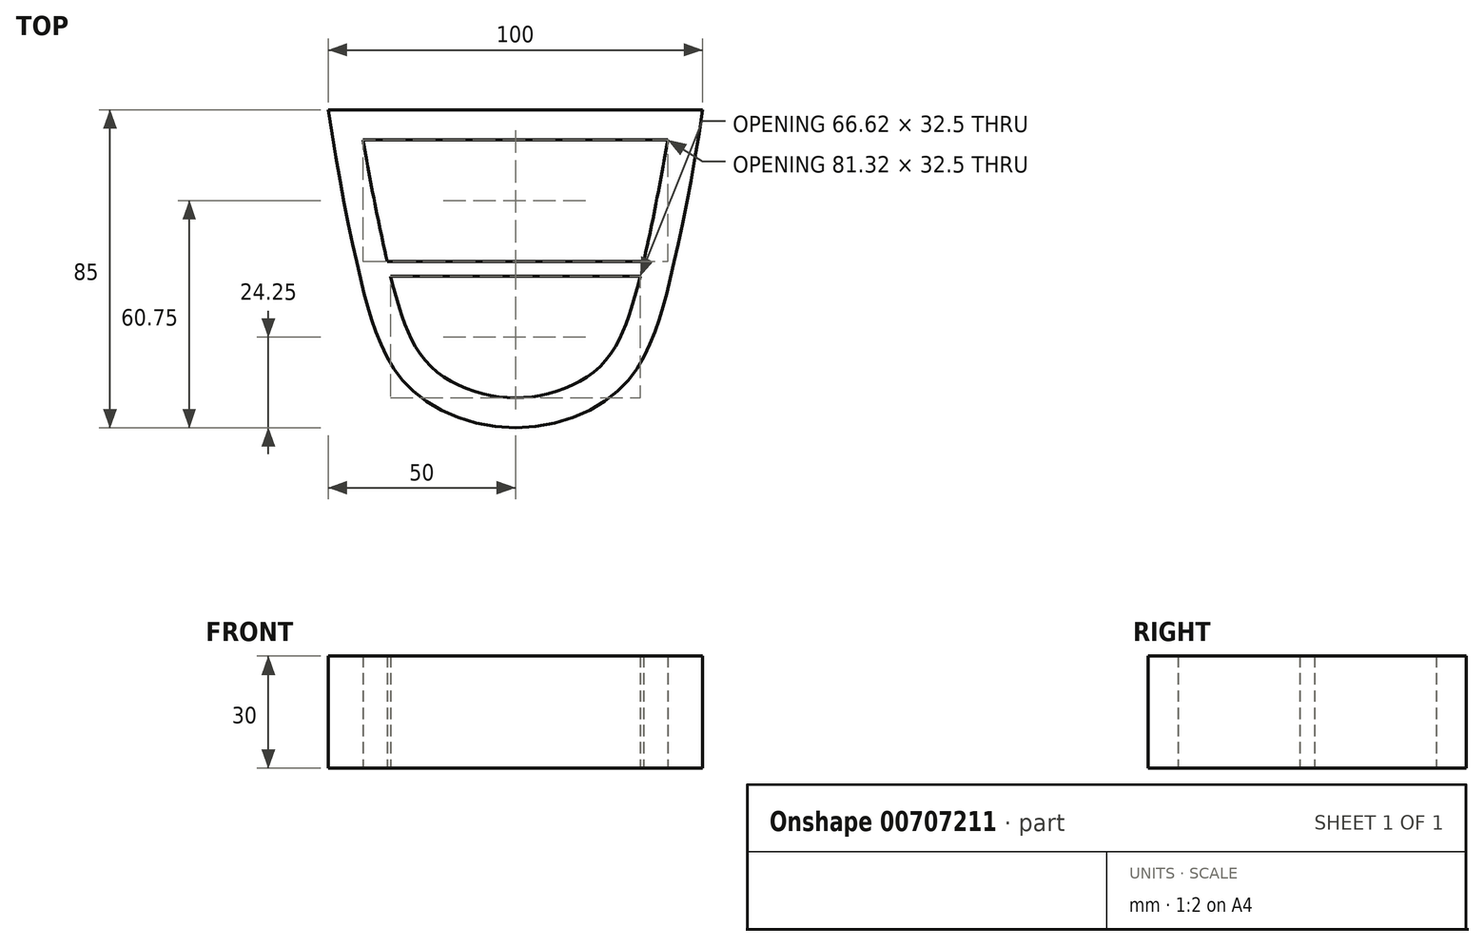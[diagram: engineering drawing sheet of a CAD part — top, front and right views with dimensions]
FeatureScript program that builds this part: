
annotation { "Feature Type Name" : "Feature", "Feature Type Description" : "" }
export const myFeature = defineFeature(function(context is Context, id is Id, definition is map)
    precondition{}
    {
        {
            var Q0;
            Q0=qCreatedBy(makeId("Top.planeOp"),FACE);
            var sketch = newSketch(context, id + "F0", { "sketchPlane" : qUnion([Q0])});
            skLineSegment(sketch, "E0.bottom", {"start": v(50, 42.5) * mm, "end": v(-50, 42.5) * mm});
            skLineSegment(sketch, "E0.top", {"start": v(50, -42.5) * mm, "end": v(-50, -42.5) * mm, "construction": true});
            skLineSegment(sketch, "E0.left", {"start": v(50, 42.5) * mm, "end": v(50, -42.5) * mm, "construction": true});
            skLineSegment(sketch, "E0.right", {"start": v(-50, 42.5) * mm, "end": v(-50, -42.5) * mm, "construction": true});
            skPoint(sketch, "E0.middle", {"position": v(0, 0) * mm});
            skPoint(sketch, "E1", {"position": v(0, -42.5) * mm});
            skPoint(sketch, "E2", {"position": v(-50, 0) * mm});
            skPoint(sketch, "E3", {"position": v(50, 0) * mm});
            skLineSegment(sketch, "E4", {"start": v(-50, 0) * mm, "end": v(-42, 0) * mm, "construction": true});
            skLineSegment(sketch, "E5", {"start": v(-42, 0) * mm, "end": v(42, 0) * mm, "construction": true});
            skLineSegment(sketch, "E6", {"start": v(42, 0) * mm, "end": v(50, 0) * mm, "construction": true});
            skLineSegment(sketch, "E7", {"start": v(-50, 0) * mm, "end": v(-50, -17.5) * mm, "construction": true});
            skLineSegment(sketch, "E8", {"start": v(-50, -17.5) * mm, "end": v(-37, -17.5) * mm, "construction": true});
            skLineSegment(sketch, "E9", {"start": v(-37, -17.5) * mm, "end": v(37, -17.5) * mm, "construction": true});
            skLineSegment(sketch, "E10", {"start": v(-50, -42.5) * mm, "end": v(-50, -32.5) * mm, "construction": true});
            skLineSegment(sketch, "E11", {"start": v(-50, -32.5) * mm, "end": v(-27.5, -32.5) * mm, "construction": true});
            skLineSegment(sketch, "E12", {"start": v(-27.5, -32.5) * mm, "end": v(27.5, -32.5) * mm, "construction": true});
            skFitSpline(sketch, "E13", {"points": [v(-50, 42.5) * mm, v(-42, 0) * mm, v(-37, -17.5) * mm, v(-27.5, -32.5) * mm, v(0, -42.5) * mm], "startDerivative": vector(21.42, -147.83) * mm, "endDerivative": vector(126.05, 0) * mm});
            skFitSpline(sketch, "E14.MirrorCS", {"points": [v(50, 42.5) * mm, v(42, 0) * mm, v(37, -17.5) * mm, v(27.5, -32.5) * mm, v(0, -42.5) * mm], "startDerivative": vector(-21.42, -147.83) * mm, "endDerivative": vector(-126.05, 0) * mm});
            skSolve(sketch);
        }
        {
            var Q0;
            Q0 = qSketchRegion(id + "F0", true);
            extrude(context, id + "F1", {"entities" : qUnion([Q0]), "depth" : 30 * mm, "offsetDistance" : 25 * mm});
        }
        {
            var Q0;
            Q0=makeQuery(id+"F1.opExtrude","CAP_FACE",FACE,{"disambiguationData":[OSD([sQuery(id+"F0.wireOp",EDGE,"E0.bottom"),sQuery(id+"F0.wireOp",EDGE,"E13"),sQuery(id+"F0.wireOp",EDGE,"E14.MirrorCS")])],"isStart":false});
            var Q1;
            Q1=makeQuery(id+"F1.opExtrude","CAP_FACE",FACE,{"disambiguationData":[OSD([sQuery(id+"F0.wireOp",EDGE,"E0.bottom"),sQuery(id+"F0.wireOp",EDGE,"E13"),sQuery(id+"F0.wireOp",EDGE,"E14.MirrorCS")])],"isStart":true});
            shell(context, id + "F2", {"entities" : qUnion([Q0, Q1]), "thickness" : 8 * mm});
        }
        {
            var Q0;
            Q0=qCreatedBy(makeId("Top.planeOp"),FACE);
            var sketch = newSketch(context, id + "F3", { "sketchPlane" : qUnion([Q0])});
            skLineSegment(sketch, "E15.bottom", {"start": v(40, 2) * mm, "end": v(-40, 2) * mm});
            skLineSegment(sketch, "E15.top", {"start": v(40, -2) * mm, "end": v(-40, -2) * mm});
            skLineSegment(sketch, "E15.left", {"start": v(40, 2) * mm, "end": v(40, -2) * mm});
            skLineSegment(sketch, "E15.right", {"start": v(-40, 2) * mm, "end": v(-40, -2) * mm});
            skPoint(sketch, "E15.middle", {"position": v(0, 0) * mm});
            skSolve(sketch);
        }
        {
            var Q0;
            Q0 = qSketchRegion(id + "F3", true);
            extrude(context, id + "F4", {"entities" : qUnion([Q0]), "operationType" : NewBodyOperationType.ADD, "depth" : 30 * mm, "offsetDistance" : 25 * mm});
        }
    });
